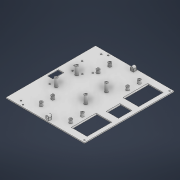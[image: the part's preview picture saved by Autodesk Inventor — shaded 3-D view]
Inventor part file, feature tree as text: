
AUTODESK INVENTOR PART (.ipt)
format: ipt  version: 2021 (Build 250183000, 183)  size: 550,912 bytes
history: native  units: mm
features: extrude x13, sketch x10, projected_geometry x8, fillet x4, other x1
ambient origin geometry x8: Origin, YZ Plane, XZ Plane, XY Plane, X Axis, Y Axis, Z Axis, Center Point
bodies: Volumenkörper1 (feature_tree)
feature tree (36):
  other  "Obenplatte_hinten"
  extrude  "Extrusion1"  Depth=200.0mm
  extrude  "Extrusion2"  Depth=2.0mm
  extrude  "Extrusion4"  Depth=5.0mm
  extrude  "Extrusion5"  Depth=2.0mm TaperAngle=0.0deg
  fillet  "Rundung1"  Radius=3.2mm
  fillet  "Rundung2"  Radius=23.0mm
  sketch  "Skizze5"  dims[d28=10.5mm d29=3.2mm]
  extrude  "Extrusion6"  Depth=3.2mm
  extrude  "Extrusion8"  Depth=74.5mm
  fillet  "Rundung3"  Radius=3.2mm
  extrude  "Extrusion9"  Depth=74.5mm
  extrude  "Extrusion7"  Depth=10.5mm
  extrude  "Extrusion10"  Depth=10.0mm TaperAngle=0.0deg
  extrude  "Extrusion11"  Depth=5.0mm
  extrude  "Extrusion12"  Depth=10.0mm
  extrude  "Extrusion13"  Depth=24.0mm
  extrude  "Extrusion14"  Depth=5.0mm
  fillet  "Rundung4"  Radius=88.0mm
  sketch  "Skizze1"  dims[d0=175.0mm d1=200.0mm]
  sketch  "Skizze2"  dims[d2=2.0mm d3=0.0mm d4=3.2mm]
  sketch  "Skizze3"  dims[d6=5.0mm d7=3.2mm]
  sketch  "Skizze4"  dims[d9=5.0mm d10=2.0mm d11=0.0mm d26=3.2mm d27=23.0mm]
  sketch  "Skizze6"  dims[d30=23.0mm d31=74.5mm d32=3.2mm]
  projected_geometry  "Projizierte Kontur1"
  projected_geometry  "Projizierte Kontur2"
  projected_geometry  "Projizierte Kontur3"
  projected_geometry  "Projizierte Kontur4"
  sketch  "Skizze8"  dims[d33=23.0mm d34=74.5mm]
  projected_geometry  "Projizierte Kontur5"
  projected_geometry  "Projizierte Kontur6"
  projected_geometry  "Projizierte Kontur7"
  projected_geometry  "Projizierte Kontur8"
  sketch  "Skizze10"  dims[d35=3.2mm d36=10.5mm]
  sketch  "Skizze11"  dims[d37=23.0mm d38=10.0mm d39=0.0mm]
  sketch  "Skizze12"  dims[d40=33.0mm d41=5.0mm d42=10.0mm d43=24.0mm d44=5.0mm d45=88.0mm d46=10.0mm d47=0.0mm d48=2.0mm d49=2.0mm d50=7.0mm d51=7.0mm d52=7.0mm d53=7.0mm d54=23.5mm d55=23.5mm d56=55.0mm d57=66.0mm d58=55.0mm d59=66.0mm d60=26.0mm d61=26.0mm d62=33.0mm d63=12.0mm d64=15.0mm d65=55.0mm d66=7.0mm d67=0.0mm d68=4.0mm d69=4.0mm d70=4.0mm d71=4.0mm d72=4.0mm d73=4.0mm d74=4.0mm d75=4.0mm d76=5.0mm d77=0.0mm d78=5.0mm d79=0.0mm d80=2.0mm d81=7.0mm d82=7.0mm d83=7.0mm d84=7.0mm d85=35.0mm d86=35.0mm d87=46.0mm d88=46.0mm d89=23.0mm d90=23.0mm d91=66.0mm d92=66.0mm d93=25.0mm d94=30.0mm d95=9.0mm d96=18.0mm d97=0.0mm d98=4.0mm d99=4.0mm d100=4.0mm d101=4.0mm d102=5.0mm d103=0.0mm d104=3.2mm d105=3.2mm d106=13.8mm d107=0.2mm d108=6.8mm d109=3.2mm d110=3.2mm d111=15.0mm d112=15.0mm d113=17.0mm d115=10.0mm d116=0.0mm d117=7.0mm d118=7.0mm d119=2.2mm d120=81.5mm d121=9.0mm d122=0.0mm d123=4.0mm d124=5.0mm d125=3.5mm d126=5.0mm d127=0.0mm d128=4.0mm d129=5.0mm d130=3.5mm d131=5.0mm d132=0.0mm d133=3.5mm d134=55.897306mm d135=49.854048mm d136=40.145952mm d137=45.0mm d138=1.5mm d139=1.5mm]
